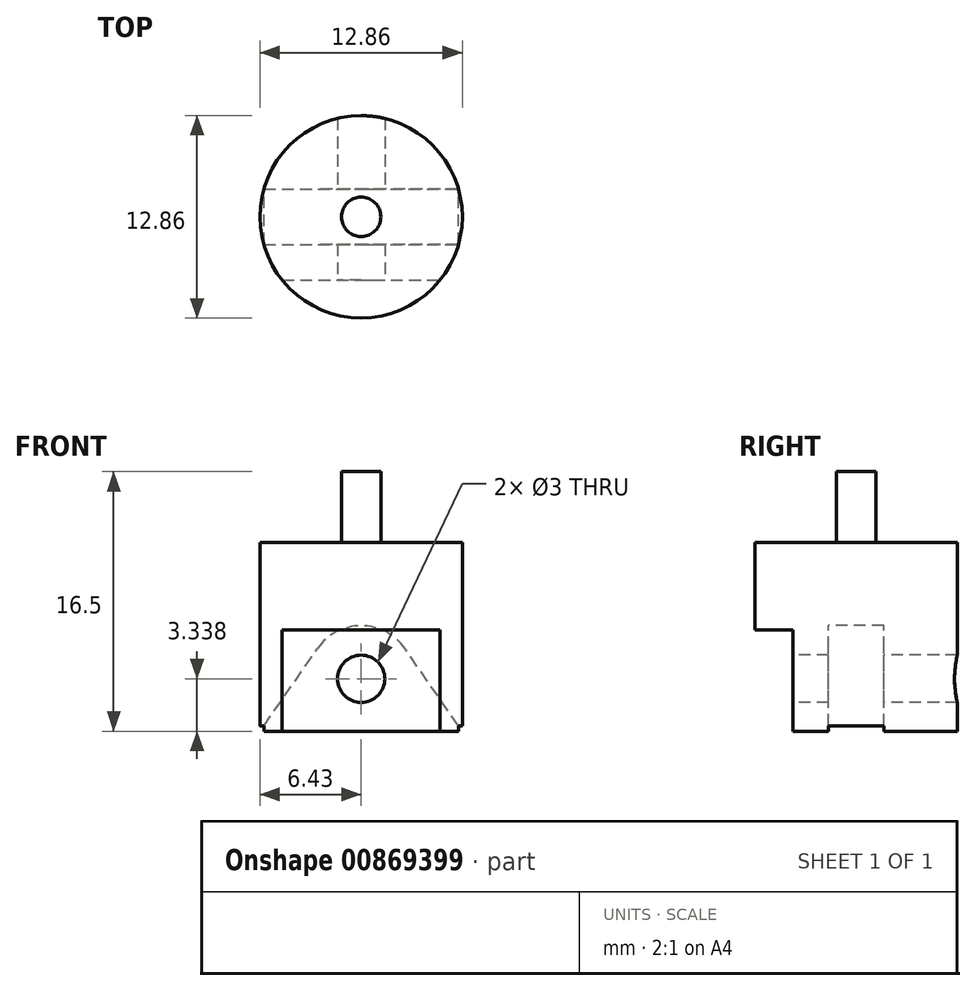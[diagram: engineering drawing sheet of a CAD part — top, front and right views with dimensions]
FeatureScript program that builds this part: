
annotation { "Feature Type Name" : "Feature", "Feature Type Description" : "" }
export const myFeature = defineFeature(function(context is Context, id is Id, definition is map)
    precondition{}
    {
        {
            var Q0;
            Q0=qCreatedBy(makeId("Top.planeOp"),FACE);
            var sketch = newSketch(context, id + "F0", { "sketchPlane" : qUnion([Q0])});
            skCircle(sketch, "E0", {"center": v(0, 0) * mm, "radius": 6.42 * mm});
            skSolve(sketch);
        }
        {
            var Q0;
            Q0=qSketchRegion(id+"F0",true);
            extrude(context, id + "F1", {"entities" : qUnion([Q0]), "oppositeDirection" : true, "depth" : 12 * mm, "offsetDistance" : 25 * mm});
        }
        {
            var Q0;
            Q0=qCreatedBy(makeId("Front.planeOp"),FACE);
            var sketch = newSketch(context, id + "F2", { "sketchPlane" : qUnion([Q0])});
            skCircle(sketch, "E1", {"center": v(0, -8.66) * mm, "radius": 1.5 * mm});
            skSolve(sketch);
        }
        {
            var Q0;
            Q0=qSketchRegion(id+"F2",true);
            extrude(context, id + "F3", {"entities" : qUnion([Q0]), "operationType" : NewBodyOperationType.REMOVE, "endBound" : BoundingType.SYMMETRIC, "oppositeDirection" : true, "depth" : 25 * mm, "offsetDistance" : 25 * mm});
        }
        {
            var Q0;
            Q0=qCreatedBy(makeId("Front.planeOp"),FACE);
            var sketch = newSketch(context, id + "F4", { "sketchPlane" : qUnion([Q0])});
            skArc(sketch, "E2", {"start": v(2.77, -6.74) * mm, "mid": v(0, -5.29) * mm, "end": v(-2.77, -6.74) * mm});
            skLineSegment(sketch, "E3.0", {"start": v(-6.42, -12) * mm, "end": v(6.42, -12) * mm});
            skLineSegment(sketch, "E4", {"start": v(6.43, -12) * mm, "end": v(2.77, -6.74) * mm});
            skLineSegment(sketch, "E5", {"start": v(-6.43, -12) * mm, "end": v(-2.77, -6.74) * mm});
            skSolve(sketch);
        }
        {
            var Q0;
            Q0=qSketchRegion(id+"F4",true);
            extrude(context, id + "F5", {"entities" : qUnion([Q0]), "operationType" : NewBodyOperationType.REMOVE, "endBound" : BoundingType.SYMMETRIC, "oppositeDirection" : true, "depth" : 3.5 * mm, "offsetDistance" : 25 * mm});
        }
        {
            var Q0;
            Q0=qCreatedBy(makeId("Right.planeOp"),FACE);
            var sketch = newSketch(context, id + "F6", { "sketchPlane" : qUnion([Q0])});
            skLineSegment(sketch, "E6", {"start": v(-6.42, -12) * mm, "end": v(-6.42, -5.56) * mm});
            skLineSegment(sketch, "E7", {"start": v(-4.03, -12) * mm, "end": v(-4.03, -5.56) * mm});
            skLineSegment(sketch, "E8", {"start": v(-4.03, -5.56) * mm, "end": v(-6.42, -5.56) * mm});
            skLineSegment(sketch, "E9", {"start": v(-6.42, -7.16) * mm, "end": v(-4.03, -7.16) * mm});
            skLineSegment(sketch, "E10", {"start": v(-4.03, -10.16) * mm, "end": v(-6.42, -10.16) * mm});
            skPoint(sketch, "E11.orphan", {"position": v(-6.42, -12) * mm});
            skPoint(sketch, "E12.0.start.orphan", {"position": v(-1.75, -12) * mm});
            skPoint(sketch, "E13.orphan", {"position": v(0, -10.16) * mm});
            skPoint(sketch, "E14.orphan", {"position": v(0, -7.16) * mm});
            skLineSegment(sketch, "E15", {"start": v(-6.42, -10.16) * mm, "end": v(-6.42, -12) * mm});
            skLineSegment(sketch, "E16", {"start": v(-4.03, -12) * mm, "end": v(-6.42, -12) * mm});
            skLineSegment(sketch, "E17.0", {"start": v(-1.75, -11.65) * mm, "end": v(-1.75, -12) * mm});
            skLineSegment(sketch, "E18.0", {"start": v(1.75, -11.65) * mm, "end": v(1.75, -12) * mm});
            skLineSegment(sketch, "E19", {"start": v(-1.75, -11.65) * mm, "end": v(1.75, -11.65) * mm});
            skLineSegment(sketch, "E20", {"start": v(-1.75, -12) * mm, "end": v(1.75, -12) * mm});
            skSolve(sketch);
        }
        {
            var Q0;
            {var subQ0=sQuery(id+"F6.wireOp",EDGE,"E10");var subQ6=makeQuery(id+"F6.imprint","IMPRINT",EDGE,{"derivedFrom":subQ0});var subQ7=sQuery(id+"F6.wireOp",EDGE,"E9");var subQ10=makeQuery(id+"F6.imprint","IMPRINT",EDGE,{"derivedFrom":subQ7});var subQ11=sQuery(id+"F6.wireOp",EDGE,"E8");Q0=qUnion([makeQuery(id+"F6.imprint","IMPRINT",FACE,{"disambiguationData":[TD([[makeQuery(id+"F6.imprint","IMPRINT",EDGE,{"derivedFrom":sQuery(id+"F6.wireOp",EDGE,"E17.0")}),1.0]])]}),makeQuery(id+"F6.imprint","IMPRINT",FACE,{"disambiguationData":[TD([[makeQuery(id+"F6.imprint","IMPRINT",EDGE,{"derivedFrom":subQ11}),1.0]])]}),makeQuery(id+"F6.imprint","IMPRINT",FACE,{"disambiguationData":[TD([[subQ10,-1.0]])]}),makeQuery(id+"F6.imprint","IMPRINT",FACE,{"disambiguationData":[TD([[subQ6,1.0]])]})]);}
            extrude(context, id + "F7", {"entities" : qUnion([Q0]), "operationType" : NewBodyOperationType.REMOVE, "endBound" : BoundingType.SYMMETRIC, "oppositeDirection" : true, "depth" : 25 * mm, "offsetDistance" : 25 * mm});
        }
        {
            var Q0;
            Q0=makeQuery(id+"F1.opExtrude","CAP_FACE",FACE,{"disambiguationData":[OSD([sQuery(id+"F0.wireOp",EDGE,"E0")])],"isStart":true});
            var sketch = newSketch(context, id + "F8", { "sketchPlane" : qUnion([Q0])});
            skCircle(sketch, "E21", {"center": v(0, 0) * mm, "radius": 1.25 * mm});
            skSolve(sketch);
        }
        {
            var Q0;
            Q0=makeQuery(id+"F8.imprint","IMPRINT",FACE,{"disambiguationData":[TD([[makeQuery(id+"F8.imprint","IMPRINT",EDGE,{"derivedFrom":sQuery(id+"F8.wireOp",EDGE,"E21")}),1.0]])]});
            extrude(context, id + "F9", {"entities" : qUnion([Q0]), "operationType" : NewBodyOperationType.ADD, "depth" : 4.5 * mm, "offsetDistance" : 25 * mm});
        }
    });
